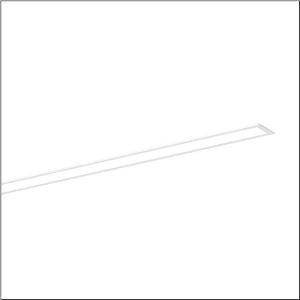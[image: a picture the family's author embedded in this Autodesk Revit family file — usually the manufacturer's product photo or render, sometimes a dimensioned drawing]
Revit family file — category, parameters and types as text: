
# Revit family: silica_r__21_51mx10dc35wb_43eb
name_source: partatom
category: Lighting Fixtures
units: mm (PartAtom-declared; Revit-internal decimal feet)

## family parameters
Cut with Voids When Loaded = No
Host = Face
Light Source = No
Part Type = Normal
Room Calculation Point = No
Round Connector Dimension = Use Diameter
Shared = No

## types (1)
- --- (1 x LED, 6000 lm, 42.6 W, 3000K)
    Apparent Load = 43 VA
    CIE Flux Codes = 48 79 96 100 100
    Color Rendering = 80
    Color Temperature = 3000K
    Default Elevation = 1800 mm
    Description = Silica® 21, office luminaire, primary optical cover: cover, of PMMA, opal, light emission: direct distribution, primary light characteristic: symmetric, installation type: recessed, LED, rated luminous flux: 6.000lm, luminous efficacy: 141lm/W, light colour: 830, colour temperature: 3000K, with terminal, 3+2-pole, max. 2.5mm², mains connection: 220..240V, AC, 50/60Hz, rated input power: 42.6W, luminaire housing, of aluminium, traffic white (RAL 9016), length: 3.028mm, width: 79mm, height: 53mm, protection rating (complete): IP20, insulation class (complete): insulation class I (protective earthing), certification: CE, permissible operating ambient temperature: 0..+35°C, standard: EN 50419, packaging unit: 1 piece
    Height = 0 mm  [stored 0 ft]
    Lamp = 1 x LED
    Lamp Light Flux = 6000 lm
    Lamp Power = 42.6 W
    Lamp count = 1
    Length = 3027 mm
    Luminous efficacy = 141 lm/W
    Manufacturer = Siteco
    ModVariant = No
    Model = 51MX10DC35WB
    Mounting Place = Ceiling
    Mounting Type = Recessed
    Number of Poles = 1
    OnlyDefault = Yes
    Power Factor = 1
    Product Name = Silica® 21
    Product group = office luminaire | ceiling recessed
    ProductGroupID = 400
    Protection Class = Protection class I
    Protection Degree = IP 20
    RLX_Detail_Level = 1
    RLX_Emergency_Light_Flux = 0 lm
    RLX_Emergency_Type = 0
    RLX_Emergency_Type_DB = No
    RlxData = <blob elided: 21197 chars, md5=9472b7eb>
    Socket = socket
    Standby Power = 0 W
    System Light Flux = 6000 lm
    System Power = 43 W
    Type Comments = factory setting: luminous flux: 100 % | dim-lin: 254 | 233 mA
    Type Image = l_1335891.jpg
    URL = http://relux.com
    VarID = @adj_086443
    Voltage = 0 V
    Weight = 0.00 kg
    Width = 79 mm

note: [stored X ft] marks values corroborated as IEEE doubles in the binary element streams (Revit-internal decimal feet)

## geometry (parser evidence)
native form markers: Blend x4, Sweep x10
no freeform markers — native parametric forms only
